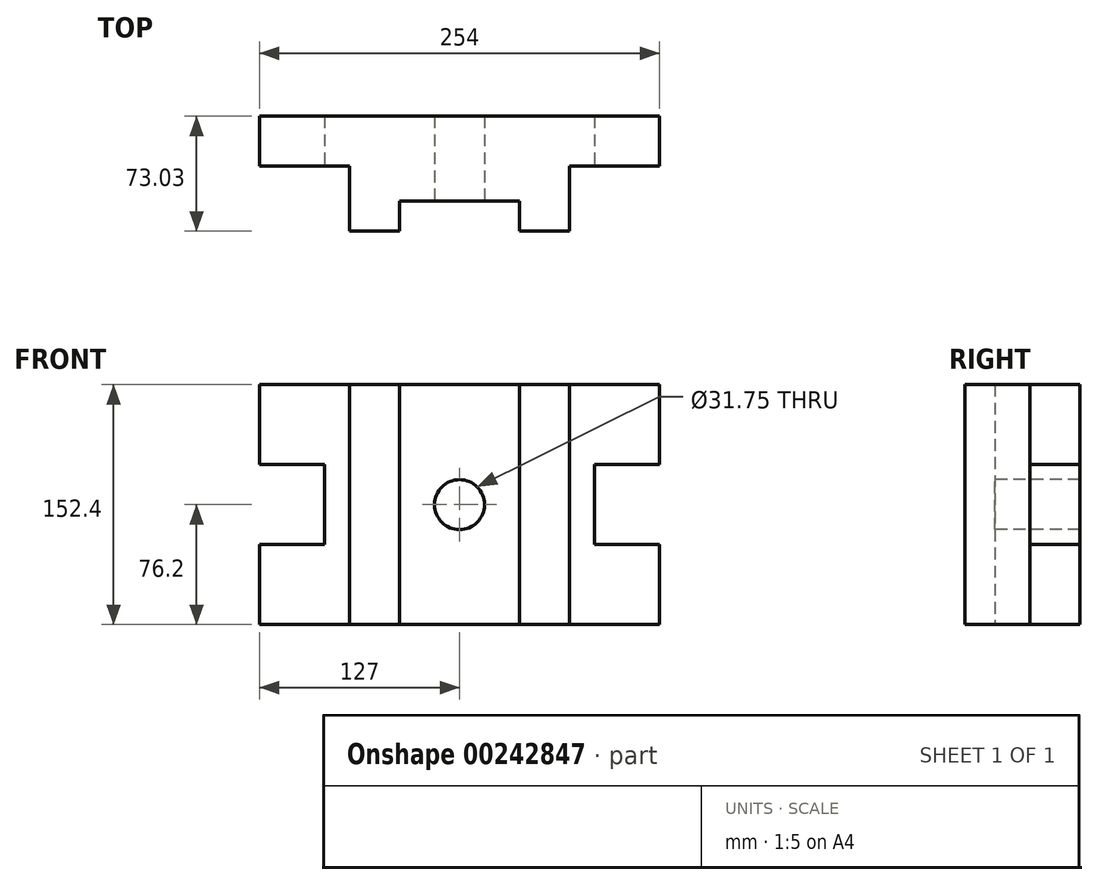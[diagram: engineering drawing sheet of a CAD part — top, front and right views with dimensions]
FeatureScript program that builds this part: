
annotation { "Feature Type Name" : "Feature", "Feature Type Description" : "" }
export const myFeature = defineFeature(function(context is Context, id is Id, definition is map)
    precondition{}
    {
        {
            var Q0;
            Q0=qCreatedBy(makeId("Front.planeOp"),FACE);
            var sketch = newSketch(context, id + "F0", { "sketchPlane" : qUnion([Q0])});
            skLineSegment(sketch, "E0.bottom", {"start": v(-127, 76.2) * mm, "end": v(127, 76.2) * mm});
            skLineSegment(sketch, "E0.top", {"start": v(-127, -76.2) * mm, "end": v(127, -76.2) * mm});
            skLineSegment(sketch, "E0.left", {"start": v(-127, 76.2) * mm, "end": v(-127, 25.4) * mm});
            skLineSegment(sketch, "E0.right", {"start": v(127, 76.2) * mm, "end": v(127, 25.4) * mm});
            skLineSegment(sketch, "E1", {"start": v(-127, -25.4) * mm, "end": v(-85.72, -25.4) * mm});
            skLineSegment(sketch, "E2", {"start": v(-85.72, -25.4) * mm, "end": v(-85.72, 25.4) * mm});
            skLineSegment(sketch, "E3", {"start": v(-85.72, 25.4) * mm, "end": v(-127, 25.4) * mm});
            skPoint(sketch, "E4", {"position": v(-127, 25.4) * mm});
            skPoint(sketch, "E5", {"position": v(-127, -25.4) * mm});
            skLineSegment(sketch, "E6", {"start": v(127, -25.4) * mm, "end": v(85.72, -25.4) * mm});
            skLineSegment(sketch, "E7", {"start": v(85.72, -25.4) * mm, "end": v(85.72, 25.4) * mm});
            skLineSegment(sketch, "E8", {"start": v(85.72, 25.4) * mm, "end": v(127, 25.4) * mm});
            skLineSegment(sketch, "E9.trimOffspring", {"start": v(-127, -25.4) * mm, "end": v(-127, -76.2) * mm});
            skLineSegment(sketch, "E10.trimOffspring", {"start": v(127, -25.4) * mm, "end": v(127, -76.2) * mm});
            skLineSegment(sketch, "E11.bottom", {"start": v(-69.85, 76.2) * mm, "end": v(-38.1, 76.2) * mm});
            skLineSegment(sketch, "E11.top", {"start": v(-69.85, -76.2) * mm, "end": v(-38.1, -76.2) * mm});
            skLineSegment(sketch, "E11.left", {"start": v(-69.85, 76.2) * mm, "end": v(-69.85, -76.2) * mm});
            skLineSegment(sketch, "E11.right", {"start": v(-38.1, 76.2) * mm, "end": v(-38.1, -76.2) * mm});
            skLineSegment(sketch, "E12.bottom", {"start": v(69.85, 76.2) * mm, "end": v(38.1, 76.2) * mm});
            skLineSegment(sketch, "E12.top", {"start": v(69.85, -76.2) * mm, "end": v(38.1, -76.2) * mm});
            skLineSegment(sketch, "E12.left", {"start": v(69.85, 76.2) * mm, "end": v(69.85, -76.2) * mm});
            skLineSegment(sketch, "E12.right", {"start": v(38.1, 76.2) * mm, "end": v(38.1, -76.2) * mm});
            skLineSegment(sketch, "E13.top", {"start": v(-69.85, 44.45) * mm, "end": v(-38.1, 44.45) * mm});
            skLineSegment(sketch, "E13.right", {"start": v(-38.1, 76.2) * mm, "end": v(-38.1, 44.45) * mm});
            skLineSegment(sketch, "E14.top", {"start": v(-69.85, -44.45) * mm, "end": v(-38.1, -44.45) * mm});
            skLineSegment(sketch, "E14.left", {"start": v(-69.85, -76.2) * mm, "end": v(-69.85, -44.45) * mm});
            skLineSegment(sketch, "E14.right", {"start": v(-38.1, -76.2) * mm, "end": v(-38.1, -44.45) * mm});
            skLineSegment(sketch, "E15.bottom", {"start": v(38.1, 76.2) * mm, "end": v(69.85, 76.2) * mm});
            skLineSegment(sketch, "E15.top", {"start": v(38.1, 44.45) * mm, "end": v(69.85, 44.45) * mm});
            skLineSegment(sketch, "E15.left", {"start": v(38.1, 76.2) * mm, "end": v(38.1, 44.45) * mm});
            skLineSegment(sketch, "E15.right", {"start": v(69.85, 76.2) * mm, "end": v(69.85, 44.45) * mm});
            skLineSegment(sketch, "E16.bottom", {"start": v(38.1, -76.2) * mm, "end": v(69.85, -76.2) * mm});
            skLineSegment(sketch, "E16.top", {"start": v(38.1, -44.45) * mm, "end": v(69.85, -44.45) * mm});
            skLineSegment(sketch, "E16.left", {"start": v(38.1, -76.2) * mm, "end": v(38.1, -44.45) * mm});
            skLineSegment(sketch, "E16.right", {"start": v(69.85, -76.2) * mm, "end": v(69.85, -44.45) * mm});
            skCircle(sketch, "E17", {"center": v(0, 0) * mm, "radius": 15.88 * mm});
            skSolve(sketch);
        }
        {
            var Q0;
            Q0=makeQuery(id+"F0.imprint","IMPRINT",FACE,{"disambiguationData":[TD([[makeQuery(id+"F0.imprint","IMPRINT",EDGE,{"derivedFrom":sQuery(id+"F0.wireOp",EDGE,"E13.bottom")}),-1.0]])]});
            var Q1;
            {var subQ0=sQuery(id+"F0.wireOp",EDGE,"E0.left");Q1=makeQuery(id+"F0.imprint","IMPRINT",FACE,{"disambiguationData":[TD([[makeQuery(id+"F0.imprint","IMPRINT",EDGE,{"derivedFrom":subQ0}),1.0]])]});}
            var Q2;
            {var subQ0=sQuery(id+"F0.wireOp",EDGE,"E0.right");Q2=makeQuery(id+"F0.imprint","IMPRINT",FACE,{"disambiguationData":[TD([[makeQuery(id+"F0.imprint","IMPRINT",EDGE,{"derivedFrom":subQ0}),-1.0]])]});}
            var Q3;
            Q3=makeQuery(id+"F0.imprint","IMPRINT",FACE,{"disambiguationData":[TD([[makeQuery(id+"F0.imprint","IMPRINT",EDGE,{"derivedFrom":sQuery(id+"F0.wireOp",EDGE,"E11.top")}),1.0]])]});
            var Q4;
            Q4=makeQuery(id+"F0.imprint","IMPRINT",FACE,{"disambiguationData":[TD([[makeQuery(id+"F0.imprint","IMPRINT",EDGE,{"derivedFrom":sQuery(id+"F0.wireOp",EDGE,"E16.bottom")}),1.0]])]});
            var Q5;
            Q5=makeQuery(id+"F0.imprint","IMPRINT",FACE,{"disambiguationData":[TD([[makeQuery(id+"F0.imprint","IMPRINT",EDGE,{"derivedFrom":sQuery(id+"F0.wireOp",EDGE,"E11.right")}),-1.0]])]});
            var Q6;
            Q6=makeQuery(id+"F0.imprint","IMPRINT",FACE,{"disambiguationData":[TD([[makeQuery(id+"F0.imprint","IMPRINT",EDGE,{"derivedFrom":sQuery(id+"F0.wireOp",EDGE,"E12.right")}),1.0]])]});
            var Q7;
            Q7=makeQuery(id+"F0.imprint","IMPRINT",FACE,{"disambiguationData":[TD([[makeQuery(id+"F0.imprint","IMPRINT",EDGE,{"derivedFrom":sQuery(id+"F0.wireOp",EDGE,"E11.right")}),1.0]])]});
            var Q8;
            Q8=makeQuery(id+"F0.imprint","IMPRINT",FACE,{"disambiguationData":[TD([[makeQuery(id+"F0.imprint","IMPRINT",EDGE,{"derivedFrom":sQuery(id+"F0.wireOp",EDGE,"E15.bottom")}),-1.0]])]});
            var Q9;
            {var subQ0=sQuery(id+"F0.wireOp",EDGE,"E11.bottom");Q9=makeQuery(id+"F0.imprint","IMPRINT",FACE,{"disambiguationData":[TD([[makeQuery(id+"F0.imprint","IMPRINT",EDGE,{"derivedFrom":subQ0}),-1.0]])]});}
            extrude(context, id + "F1", {"entities" : qUnion([Q0, Q1, Q2, Q3, Q4, Q5, Q6, Q7, Q8, Q9]), "oppositeDirection" : true, "depth" : 92.07 * mm});
        }
        {
            var Q0;
            {var subQ0=sQuery(id+"F0.wireOp",EDGE,"E0.left");Q0=makeQuery(id+"F0.imprint","IMPRINT",FACE,{"disambiguationData":[TD([[makeQuery(id+"F0.imprint","IMPRINT",EDGE,{"derivedFrom":subQ0}),1.0]])]});}
            var Q1;
            {var subQ0=sQuery(id+"F0.wireOp",EDGE,"E0.right");Q1=makeQuery(id+"F0.imprint","IMPRINT",FACE,{"disambiguationData":[TD([[makeQuery(id+"F0.imprint","IMPRINT",EDGE,{"derivedFrom":subQ0}),-1.0]])]});}
            extrude(context, id + "F2", {"entities" : qUnion([Q0, Q1]), "operationType" : NewBodyOperationType.REMOVE, "oppositeDirection" : true, "depth" : 60.32 * mm});
        }
        {
            var Q0;
            Q0=makeQuery(id+"F0.imprint","IMPRINT",FACE,{"disambiguationData":[TD([[makeQuery(id+"F0.imprint","IMPRINT",EDGE,{"derivedFrom":sQuery(id+"F0.wireOp",EDGE,"E11.right")}),1.0]])]});
            extrude(context, id + "F3", {"entities" : qUnion([Q0]), "operationType" : NewBodyOperationType.REMOVE, "oppositeDirection" : true, "depth" : 38.1 * mm});
        }
        {
            var Q0;
            Q0=makeQuery(id+"F0.imprint","IMPRINT",FACE,{"disambiguationData":[TD([[makeQuery(id+"F0.imprint","IMPRINT",EDGE,{"derivedFrom":sQuery(id+"F0.wireOp",EDGE,"E11.right")}),-1.0]])]});
            var Q1;
            Q1=makeQuery(id+"F0.imprint","IMPRINT",FACE,{"disambiguationData":[TD([[makeQuery(id+"F0.imprint","IMPRINT",EDGE,{"derivedFrom":sQuery(id+"F0.wireOp",EDGE,"E12.left")}),-1.0]])]});
            extrude(context, id + "F4", {"entities" : qUnion([Q0, Q1]), "operationType" : NewBodyOperationType.REMOVE, "oppositeDirection" : true, "depth" : 19.05 * mm});
        }
    });
